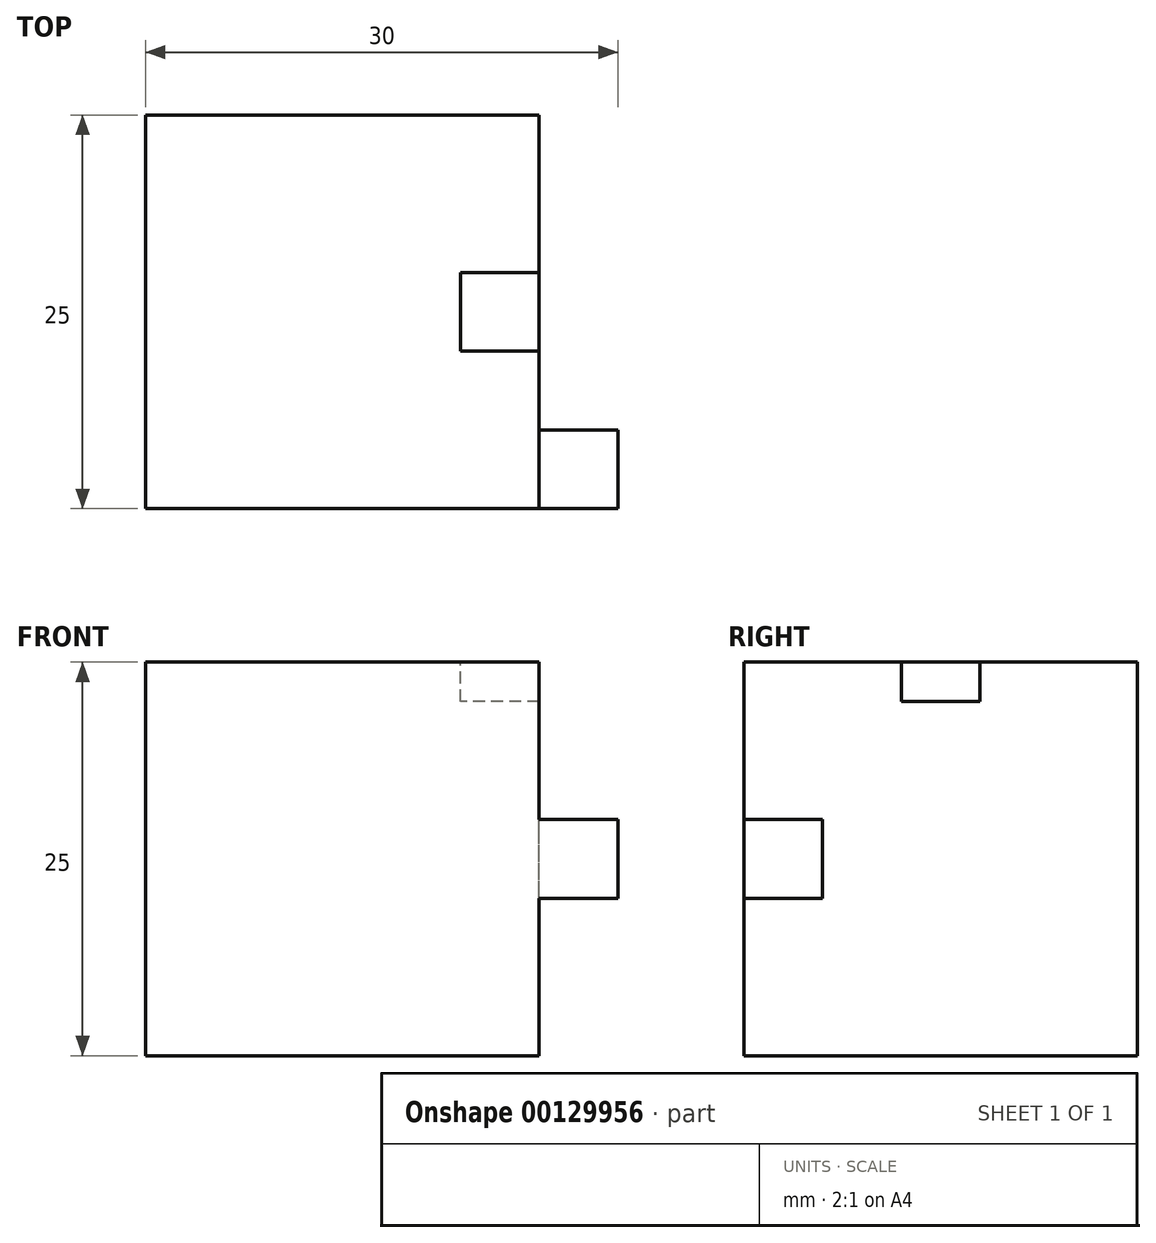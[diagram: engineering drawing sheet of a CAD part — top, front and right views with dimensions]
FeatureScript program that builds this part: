
annotation { "Feature Type Name" : "Feature", "Feature Type Description" : "" }
export const myFeature = defineFeature(function(context is Context, id is Id, definition is map)
    precondition{}
    {
        {
            var Q0;
            Q0=qCreatedBy(makeId("Front.planeOp"),FACE);
            var sketch = newSketch(context, id + "F0", { "sketchPlane" : qUnion([Q0])});
            skLineSegment(sketch, "E0.bottom", {"start": v(0, 0) * mm, "end": v(-25, 0) * mm});
            skLineSegment(sketch, "E0.top", {"start": v(0, 25) * mm, "end": v(-25, 25) * mm});
            skLineSegment(sketch, "E0.left", {"start": v(0, 0) * mm, "end": v(0, 25) * mm});
            skLineSegment(sketch, "E0.right", {"start": v(-25, 0) * mm, "end": v(-25, 25) * mm});
            skSolve(sketch);
        }
        {
            var Q0;
            Q0=makeQuery(id+"F0.imprint","IMPRINT",FACE,{"disambiguationData":[TD([[makeQuery(id+"F0.imprint","IMPRINT",EDGE,{"derivedFrom":sQuery(id+"F0.wireOp",EDGE,"E0.bottom")}),-1.0]])]});
            extrude(context, id + "F1", {"entities" : qUnion([Q0]), "depth" : 25 * mm});
        }
        {
            var Q0;
            Q0=makeQuery(id+"F1.opExtrude","CAP_FACE",FACE,{"disambiguationData":[OSD([sQuery(id+"F0.wireOp",EDGE,"E0.bottom"),sQuery(id+"F0.wireOp",EDGE,"E0.top"),sQuery(id+"F0.wireOp",EDGE,"E0.left"),sQuery(id+"F0.wireOp",EDGE,"E0.right")])],"isStart":false});
            var sketch = newSketch(context, id + "F2", { "sketchPlane" : qUnion([Q0])});
            skLineSegment(sketch, "E1", {"start": v(-15, 0) * mm, "end": v(-15, 5) * mm});
            skLineSegment(sketch, "E2", {"start": v(-15, 5) * mm, "end": v(-10, 5) * mm});
            skLineSegment(sketch, "E3", {"start": v(-10, 5) * mm, "end": v(-10, 0) * mm});
            skLineSegment(sketch, "E4", {"start": v(-25, 0) * mm, "end": v(-15, 0) * mm});
            skLineSegment(sketch, "E5", {"start": v(-10, 0) * mm, "end": v(0, 0) * mm});
            skLineSegment(sketch, "E6", {"start": v(-15, 0) * mm, "end": v(-10, 0) * mm});
            skLineSegment(sketch, "E7", {"start": v(0, 15) * mm, "end": v(5, 15) * mm});
            skLineSegment(sketch, "E8", {"start": v(5, 15) * mm, "end": v(5, 10) * mm});
            skLineSegment(sketch, "E9", {"start": v(5, 10) * mm, "end": v(0, 10) * mm});
            skLineSegment(sketch, "E10", {"start": v(0, 10) * mm, "end": v(0, 15) * mm});
            skLineSegment(sketch, "E11", {"start": v(0, 25) * mm, "end": v(0, 15) * mm});
            skLineSegment(sketch, "E12", {"start": v(0, 10) * mm, "end": v(0, 0) * mm});
            skSolve(sketch);
        }
        {
            var Q0;
            Q0=makeQuery(id+"F1.opExtrude","SWEPT_FACE",FACE,{"disambiguationData":[OSD([sQuery(id+"F0.wireOp",EDGE,"E0.top")])]});
            var sketch = newSketch(context, id + "F3", { "sketchPlane" : qUnion([Q0])});
            skLineSegment(sketch, "E13", {"start": v(-15, 0) * mm, "end": v(-15, 5) * mm});
            skLineSegment(sketch, "E14", {"start": v(-15, 5) * mm, "end": v(-10, 5) * mm});
            skLineSegment(sketch, "E15", {"start": v(-10, 5) * mm, "end": v(-10, 0) * mm});
            skLineSegment(sketch, "E16", {"start": v(-15, 0) * mm, "end": v(-25, 0) * mm});
            skLineSegment(sketch, "E17", {"start": v(-10, 0) * mm, "end": v(0, 0) * mm});
            skLineSegment(sketch, "E18", {"start": v(0, -10) * mm, "end": v(-5, -10) * mm});
            skLineSegment(sketch, "E19", {"start": v(-5, -10) * mm, "end": v(-5, -15) * mm});
            skLineSegment(sketch, "E20", {"start": v(-5, -15) * mm, "end": v(0, -15) * mm});
            skLineSegment(sketch, "E21", {"start": v(0, -10) * mm, "end": v(0, 0) * mm});
            skLineSegment(sketch, "E22", {"start": v(0, -15) * mm, "end": v(0, -25) * mm});
            skSolve(sketch);
        }
        {
            var Q0;
            Q0=makeQuery(id+"F2.imprint","IMPRINT",FACE,{"disambiguationData":[TD([[makeQuery(id+"F2.imprint","IMPRINT",EDGE,{"derivedFrom":sQuery(id+"F2.wireOp",EDGE,"E7")}),-1.0]])]});
            extrude(context, id + "F4", {"entities" : qUnion([Q0]), "operationType" : NewBodyOperationType.ADD, "oppositeDirection" : true, "depth" : 5 * mm});
        }
        {
            var Q0;
            {var subQ0=sQuery(id+"F3.wireOp",EDGE,"E18");Q0=makeQuery(id+"F3.imprint","IMPRINT",FACE,{"disambiguationData":[TD([[makeQuery(id+"F3.imprint","IMPRINT",EDGE,{"derivedFrom":subQ0}),1.0]])]});}
            extrude(context, id + "F5", {"entities" : qUnion([Q0]), "operationType" : NewBodyOperationType.REMOVE, "endBound" : BoundingType.SYMMETRIC, "oppositeDirection" : true, "depth" : 5 * mm});
        }
    });
